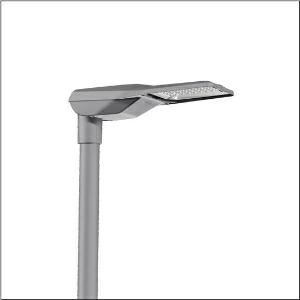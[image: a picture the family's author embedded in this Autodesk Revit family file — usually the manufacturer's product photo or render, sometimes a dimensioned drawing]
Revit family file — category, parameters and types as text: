
# Revit family: streetlight_sl_21_iq_mini___st1_0a_5xe2d41d08hb_6636
name_source: partatom
category: Lighting Fixtures
units: mm (PartAtom-declared; Revit-internal decimal feet)

## family parameters
Cut with Voids When Loaded = No
Host = Face
Light Source = No
Part Type = Normal
Room Calculation Point = No
Round Connector Dimension = Use Diameter
Shared = No

## types (1)
- --- (1 x LED, 9860 lm, 70.9 W, 4000K)
    Apparent Load = 71 VA
    CIE Flux Codes = 37 72 97 100 100
    Color Rendering = 70
    Color Temperature = 4000K
    Default Elevation = 1800 mm
    Description = Streetlight SL 21 iQ mini, mast luminaire, primary light control with lens, of PMMA, primary optical cover: cover, of toughened safety glass, transparent, light distribution: ST1.0a, light emission: direct distribution, primary light characteristic: asymmetric, installation type: post-top, side-entry, LED, High Power LED, rated luminous flux: 9.860lm, luminous efficacy: 139lm/W, light colour: 740, colour temperature: 4000K, control gear: iQ-Comfort, control: Auto-Match, Temp-Guard, Lumen-Switch, Night-Set, Smart-Wire, Light-Fading, Desk-Remote (wireless, voltage-free reading and setting of iQ features in the workshop via application-optimized NFC function/RFID function), optimised constant luminous flux control (CLO 2.0), pre-setting: linear dimming characteristic, mains connection: 220..240V, AC, 50/60Hz, start of lifetime: 71W, end of service life: 75W, reduction: 31W, luminaire housing, of diecast aluminium, powder-coated, SITECO metallic grey (DB 702S), corrosivity category C5 high according to DIN EN ISO 12944, please order mast flange separately, inclination adjustable: 0°, 5°, 10°, 15°, sealing non-destructively replaceable, multi-level sealing system, length: 628mm, width: 235mm, height: 110mm, mast flange for spigot size: 42mm (side-entry): 5XC10008XM4, 60/48mm (side-entry/post-top): 5XC10108XM2, 76/60mm (side-entry/post-top): 5XC10108XM1, mounting height: 4..8m, protection rating (complete): IP66, insulation class (complete): insulation class II (safety insulation), certification: CE, ENEC, ENEC+, VDE, impact resistance: IK10, permissible operating ambient temperature for outdoor applications: -40..+50°C, standard-compliant lighting for roads and squares, packaging unit: 1 piece

Light Distribution: ST1.0a
    Height = 110 mm
    Lamp = 1 x LED
    Lamp Light Flux = 9860 lm
    Lamp Power = 70.9 W
    Lamp count = 1
    Length = 625 mm
    Luminous efficacy = 139 lm/W
    Manufacturer = Siteco
    ModVariant = No
    Model = 5XE2D41D08HB
    Mounting Place = Pole
    Mounting Type = Pole top
    Number of Poles = 1
    OnlyDefault = Yes
    Power Factor = 1
    Product Name = Streetlight SL 21 iQ mini | ST1.0a
    Product group = mast luminaire | pylon top
    ProductGroupID = 6100
    Protection Class = Protection class II
    Protection Degree = IP 66
    RLX_Detail_Level = 1
    RLX_Emergency_Light_Flux = 0 lm
    RLX_Emergency_Type = 0
    RLX_Emergency_Type_DB = No
    RlxData = <blob elided: 26261 chars, md5=4f97e3ff>
    Socket = socket
    Standby Power = 0 W
    System Light Flux = 9860 lm
    System Power = 71 W
    Type Comments = factory setting: luminous flux: 100 % | dim-lin: 254 | 711 mA
    Type Image = l_1003519.jpg
    URL = http://relux.com
    VarID = @adj_159121
    Voltage = 0 V
    Weight = 0.00 kg
    Width = 234 mm

## geometry (parser evidence)
native form markers: Blend x4, Sweep x11
no freeform markers — native parametric forms only
